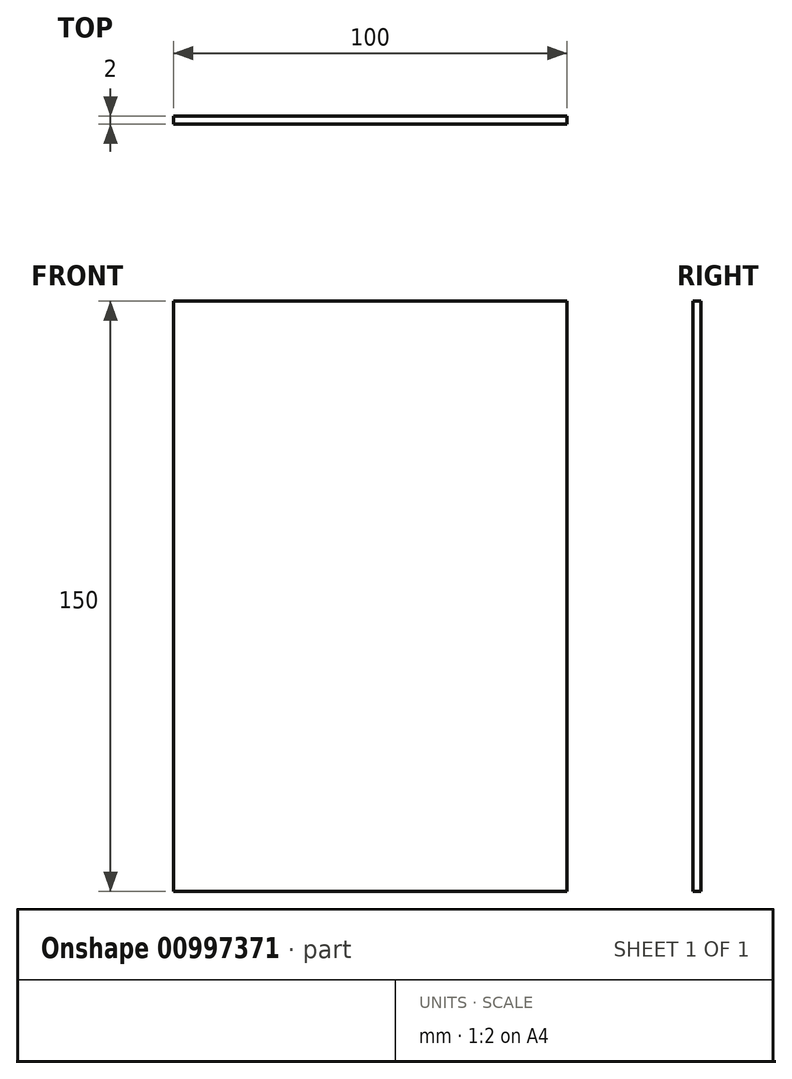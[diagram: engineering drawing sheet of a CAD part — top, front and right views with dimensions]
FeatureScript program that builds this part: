
annotation { "Feature Type Name" : "Feature", "Feature Type Description" : "" }
export const myFeature = defineFeature(function(context is Context, id is Id, definition is map)
    precondition{}
    {
        {
            var Q0;
            Q0=qCreatedBy(makeId("Front.planeOp"),FACE);
            var sketch = newSketch(context, id + "F0", { "sketchPlane" : qUnion([Q0])});
            skLineSegment(sketch, "E0.bottom", {"start": v(0, 0) * mm, "end": v(100, 0) * mm});
            skLineSegment(sketch, "E0.top", {"start": v(0, -150) * mm, "end": v(100, -150) * mm});
            skLineSegment(sketch, "E0.left", {"start": v(0, 0) * mm, "end": v(0, -150) * mm});
            skLineSegment(sketch, "E0.right", {"start": v(100, 0) * mm, "end": v(100, -150) * mm});
            skSolve(sketch);
        }
        {
            var Q0;
            Q0=makeQuery(id+"F0.imprint","IMPRINT",FACE,{"disambiguationData":[TD([[makeQuery(id+"F0.imprint","IMPRINT",EDGE,{"derivedFrom":sQuery(id+"F0.wireOp",EDGE,"E0.bottom")}),-1.0]])]});
            var Q1;
            Q1 = qSketchRegion(id + "F0", true);
            extrude(context, id + "F1", {"entities" : qUnion([Q0, Q1]), "depth" : 2 * mm, "offsetDistance" : 25 * mm});
        }
    });
